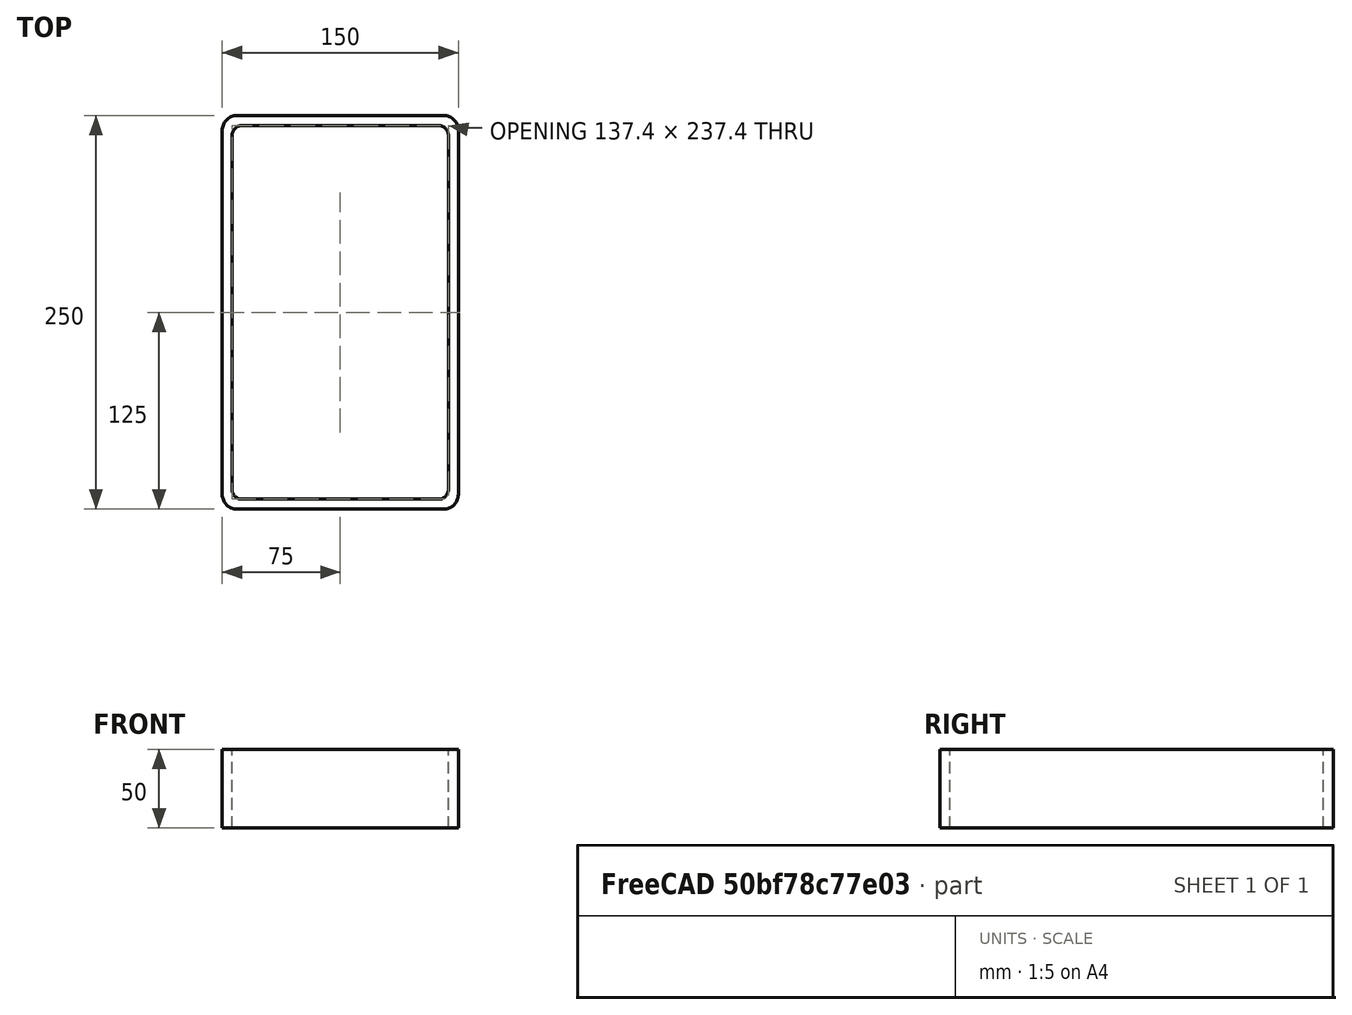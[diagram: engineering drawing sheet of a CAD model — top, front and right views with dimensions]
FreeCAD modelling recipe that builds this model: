
FCSTD DOCUMENT  (FreeCAD 0.15R4671 (Git))
Label: Rectangular hollow section 250 x150x6.3 EN10219 S235JRH
License: All rights reserved
LicenseURL: http://en.wikipedia.org/wiki/All_rights_reserved
objects: Sketcher::SketchObject×1, Part::Extrusion×1
note: 2 computed .brp shape members not serialized (recipe doc carries the construction recipe); baked Part::Feature solids carry a one-line shape summary decoded from their .brp

FEATURE [Sketcher::SketchObject] Sketch
  sketch-geometry (16):
    g0: LineSegment StartX=-62.4 StartY=118.7 StartZ=0 EndX=62.4 EndY=118.7 EndZ=0
    g1: LineSegment StartX=68.7 StartY=112.4 StartZ=0 EndX=68.7 EndY=-112.4 EndZ=0
    g2: LineSegment StartX=62.4 StartY=-118.7 StartZ=0 EndX=-62.4 EndY=-118.7 EndZ=0
    g3: LineSegment StartX=-68.7 StartY=-112.4 StartZ=0 EndX=-68.7 EndY=112.4 EndZ=0
    g4: LineSegment StartX=-65.55 StartY=125 StartZ=0 EndX=65.55 EndY=125 EndZ=0
    g5: LineSegment StartX=75 StartY=115.55 StartZ=0 EndX=75 EndY=-115.55 EndZ=0
    g6: LineSegment StartX=65.55 StartY=-125 StartZ=0 EndX=-65.55 EndY=-125 EndZ=0
    g7: LineSegment StartX=-75 StartY=-115.55 StartZ=0 EndX=-75 EndY=115.55 EndZ=0
    g8: ArcOfCircle CenterX=-62.4 CenterY=112.4 CenterZ=0 NormalX=0 NormalY=0 NormalZ=1 Radius=6.3 StartAngle=1.5708 EndAngle=3.14159
    g9: ArcOfCircle CenterX=62.4 CenterY=112.4 CenterZ=0 NormalX=0 NormalY=0 NormalZ=1 Radius=6.3 StartAngle=0 EndAngle=1.5708
    g10: ArcOfCircle CenterX=62.4 CenterY=-112.4 CenterZ=0 NormalX=0 NormalY=0 NormalZ=1 Radius=6.3 StartAngle=4.71239 EndAngle=6.28319
    g11: ArcOfCircle CenterX=-62.4 CenterY=-112.4 CenterZ=0 NormalX=0 NormalY=0 NormalZ=1 Radius=6.3 StartAngle=3.14159 EndAngle=4.71239
    g12: ArcOfCircle CenterX=65.55 CenterY=115.55 CenterZ=0 NormalX=0 NormalY=0 NormalZ=1 Radius=9.45 StartAngle=0 EndAngle=1.5708
    g13: ArcOfCircle CenterX=65.55 CenterY=-115.55 CenterZ=0 NormalX=0 NormalY=0 NormalZ=1 Radius=9.45 StartAngle=4.71239 EndAngle=6.28319
    g14: ArcOfCircle CenterX=-65.55 CenterY=-115.55 CenterZ=0 NormalX=0 NormalY=0 NormalZ=1 Radius=9.45 StartAngle=3.14159 EndAngle=4.71239
    g15: ArcOfCircle CenterX=-65.55 CenterY=115.55 CenterZ=0 NormalX=0 NormalY=0 NormalZ=1 Radius=9.45 StartAngle=1.5708 EndAngle=3.14159
  constraints (36):
    c: Horizontal(g2)
    c: Vertical(g3)
    c: Horizontal(g6)
    c: Vertical(g7)
    c: Tangent(g3,g8) = 1.5708
    c: Tangent(g0,g8) = 1.5708
    c: Tangent(g0,g9) = 1.5708
    c: Tangent(g1,g9) = 1.5708
    c: Tangent(g1,g10) = 1.5708
    c: Tangent(g2,g10) = 1.5708
    c: Tangent(g2,g11) = 1.5708
    c: Tangent(g3,g11) = 1.5708
    c: Tangent(g4,g12) = 1.5708
    c: Tangent(g5,g12) = 1.5708
    c: Tangent(g5,g13) = 1.5708
    c: Tangent(g6,g13) = 1.5708
    c: Tangent(g6,g14) = 1.5708
    c: Tangent(g7,g14) = 1.5708
    c: Tangent(g7,g15) = 1.5708
    c: Tangent(g4,g15) = 1.5708
    c: Equal(g9,g8)
    c: Equal(g9,g11)
    c: Equal(g9,g10)
    c: Equal(g12,g15)
    c: Equal(g12,g14)
    c: Equal(g12,g13)
    c: Symmetric(g4,g6,g-1)
    c: Symmetric(g7,g5,g-2)
    c: DistanceY(g4,g6) = -250
    c: DistanceX(g7,g5) = 150
    c: Symmetric(g3,g1,g-2)
    c: Symmetric(g0,g2,g-1)
    c: DistanceY(g0,g4) = 6.3
    c: DistanceX(g5,g1) = -6.3
    c: Radius(g9) = 6.3
    c: Radius(g12) = 9.45
FEATURE [Part::Extrusion] Extrude  label="Rectangular hollow section 250 x150x6.3 EN10219 S235JRH"
  Base = -> Sketch
  Dir = (0,0,50)
  Solid = true
